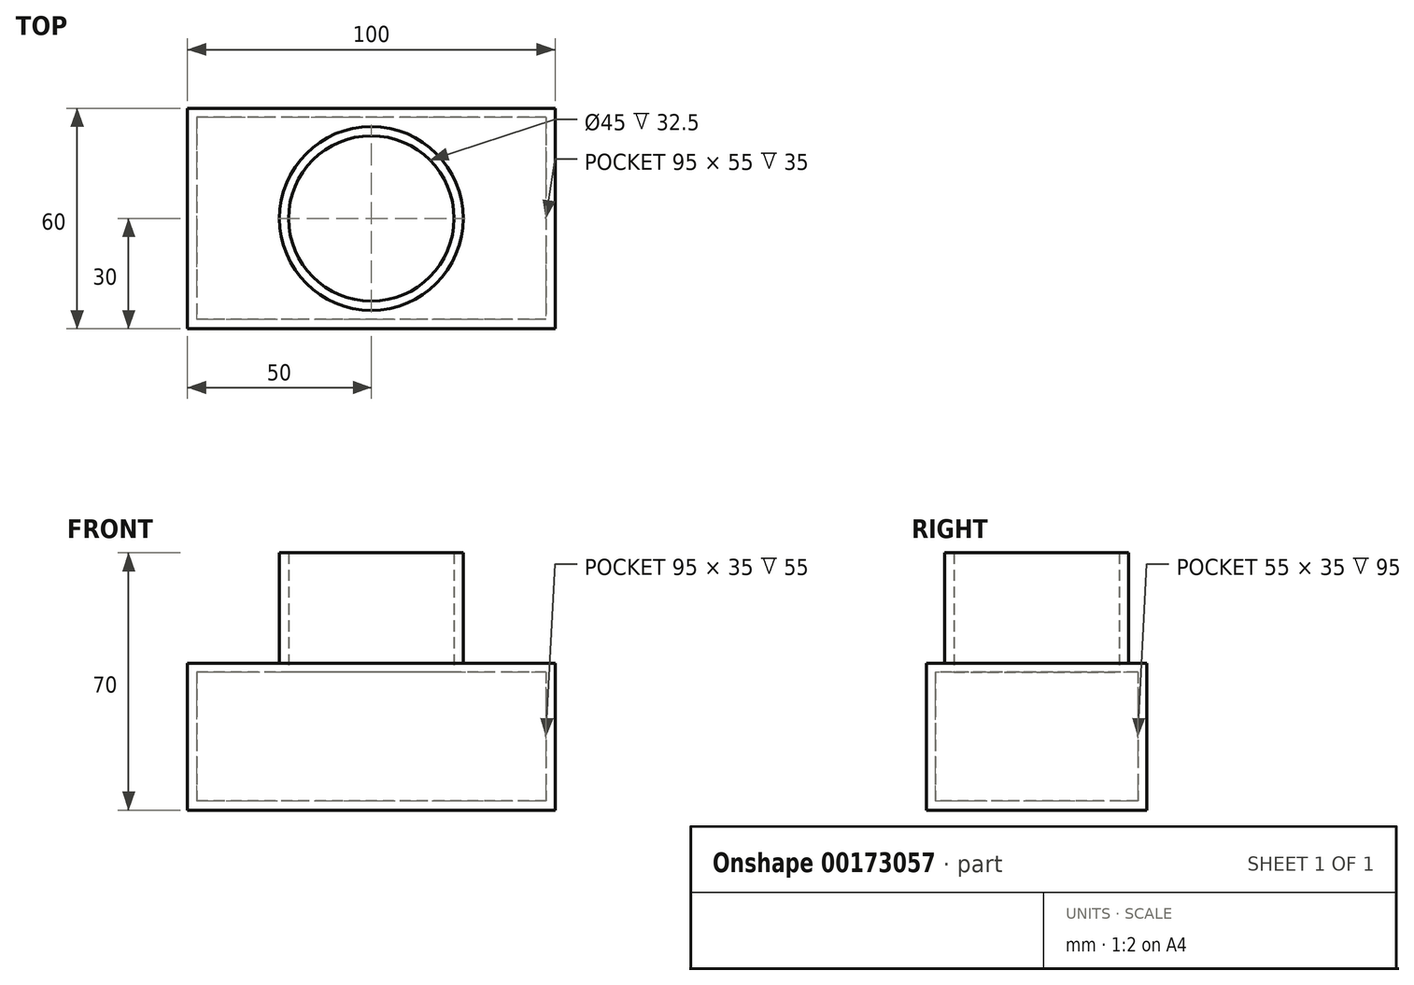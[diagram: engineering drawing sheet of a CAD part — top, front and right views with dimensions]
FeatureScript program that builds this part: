
annotation { "Feature Type Name" : "Feature", "Feature Type Description" : "" }
export const myFeature = defineFeature(function(context is Context, id is Id, definition is map)
    precondition{}
    {
        {
            var Q0;
            Q0=qCreatedBy(makeId("Top.planeOp"),FACE);
            var sketch = newSketch(context, id + "F0", { "sketchPlane" : qUnion([Q0])});
            skLineSegment(sketch, "E0.bottom", {"start": v(50, 30) * mm, "end": v(-50, 30) * mm});
            skLineSegment(sketch, "E0.top", {"start": v(50, -30) * mm, "end": v(-50, -30) * mm});
            skLineSegment(sketch, "E0.left", {"start": v(50, 30) * mm, "end": v(50, -30) * mm});
            skLineSegment(sketch, "E0.right", {"start": v(-50, 30) * mm, "end": v(-50, -30) * mm});
            skPoint(sketch, "E0.middle", {"position": v(0, 0) * mm});
            skSolve(sketch);
        }
        {
            var Q0;
            Q0 = qSketchRegion(id + "F0", true);
            extrude(context, id + "F1", {"entities" : qUnion([Q0]), "depth" : 40 * mm});
        }
        {
            var Q0;
            Q0=makeQuery(id+"F1.opExtrude","CAP_FACE",FACE,{"disambiguationData":[OSD([sQuery(id+"F0.wireOp",EDGE,"E0.bottom"),sQuery(id+"F0.wireOp",EDGE,"E0.top"),sQuery(id+"F0.wireOp",EDGE,"E0.left"),sQuery(id+"F0.wireOp",EDGE,"E0.right")])],"isStart":false});
            var sketch = newSketch(context, id + "F2", { "sketchPlane" : qUnion([Q0])});
            skCircle(sketch, "E1", {"center": v(0, 0) * mm, "radius": 25 * mm});
            skSolve(sketch);
        }
        {
            var Q0;
            Q0 = qSketchRegion(id + "F2", true);
            extrude(context, id + "F3", {"entities" : qUnion([Q0]), "operationType" : NewBodyOperationType.ADD, "depth" : 30 * mm});
        }
        {
            var Q0;
            Q0=makeQuery(id+"F3.opExtrude","CAP_FACE",FACE,{"disambiguationData":[OSD([sQuery(id+"F2.wireOp",EDGE,"E1")])],"isStart":false});
            shell(context, id + "F4", {"entities" : qUnion([Q0]), "thickness" : 2.5 * mm});
        }
    });
